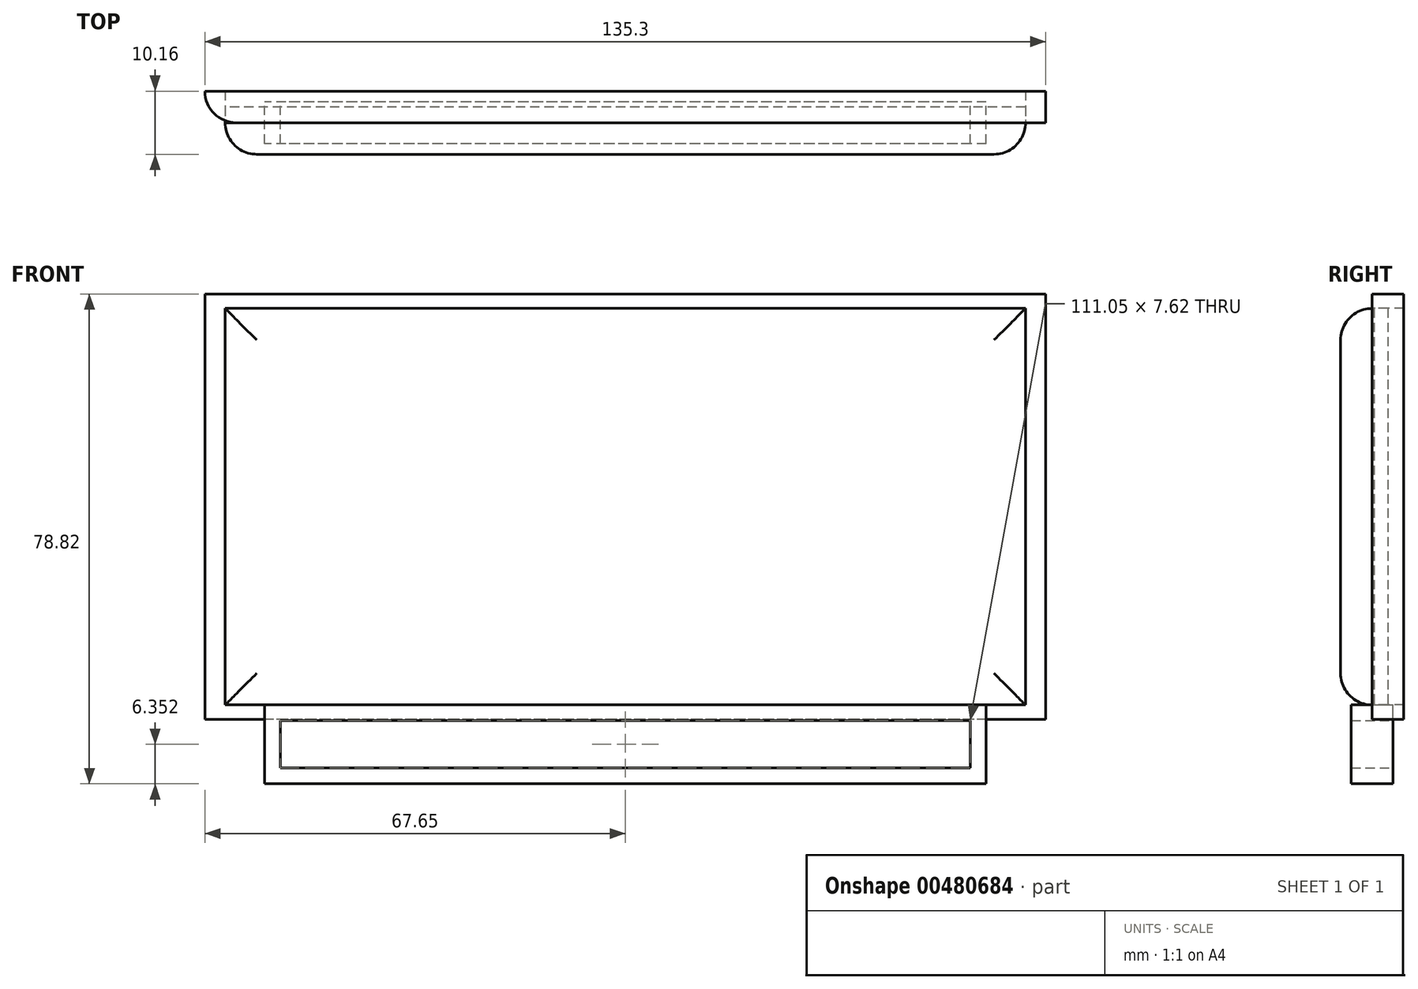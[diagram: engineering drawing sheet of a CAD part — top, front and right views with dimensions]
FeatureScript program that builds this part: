
annotation { "Feature Type Name" : "Feature", "Feature Type Description" : "" }
export const myFeature = defineFeature(function(context is Context, id is Id, definition is map)
    precondition{}
    {
        {
            var Q0;
            Q0=qCreatedBy(makeId("Front.planeOp"),FACE);
            var sketch = newSketch(context, id + "F0", { "sketchPlane" : qUnion([Q0])});
            skLineSegment(sketch, "E0.bottom", {"start": v(67.65, 34.2) * mm, "end": v(-67.65, 34.2) * mm});
            skLineSegment(sketch, "E0.top", {"start": v(67.65, -34.2) * mm, "end": v(-67.65, -34.2) * mm});
            skLineSegment(sketch, "E0.left", {"start": v(67.65, 34.2) * mm, "end": v(67.65, -34.2) * mm});
            skLineSegment(sketch, "E0.right", {"start": v(-67.65, 34.2) * mm, "end": v(-67.65, -34.2) * mm});
            skPoint(sketch, "E0.middle", {"position": v(0, 0) * mm});
            skLineSegment(sketch, "E1.bottom", {"start": v(64.4, 31.9) * mm, "end": v(-64.4, 31.9) * mm});
            skLineSegment(sketch, "E1.top", {"start": v(64.4, -31.9) * mm, "end": v(-64.4, -31.9) * mm});
            skLineSegment(sketch, "E1.left", {"start": v(64.4, 31.9) * mm, "end": v(64.4, -31.9) * mm});
            skLineSegment(sketch, "E1.right", {"start": v(-64.4, 31.9) * mm, "end": v(-64.4, -31.9) * mm});
            skSolve(sketch);
        }
        {
            var Q0;
            Q0=makeQuery(id+"F0.imprint","IMPRINT",FACE,{"disambiguationData":[TD([[makeQuery(id+"F0.imprint","IMPRINT",EDGE,{"derivedFrom":sQuery(id+"F0.wireOp",EDGE,"E1.bottom")}),1.0]])]});
            extrude(context, id + "F1", {"entities" : qUnion([Q0]), "depth" : 5.08 * mm});
        }
        {
            var Q0;
            Q0 = qSketchRegion(id + "F0", true);
            extrude(context, id + "F2", {"entities" : qUnion([Q0]), "oppositeDirection" : true, "depth" : 5.08 * mm});
        }
        {
            var Q0;
            Q0=makeQuery(id+"F1.opExtrude","SWEPT_FACE",FACE,{"disambiguationData":[OSD([sQuery(id+"F0.wireOp",EDGE,"E1.top")])]});
            var sketch = newSketch(context, id + "F3", { "sketchPlane" : qUnion([Q0])});
            skLineSegment(sketch, "E2.bottom", {"start": v(58.07, 3.35) * mm, "end": v(-58.07, 3.35) * mm});
            skLineSegment(sketch, "E2.top", {"start": v(58.07, -3.35) * mm, "end": v(-58.07, -3.35) * mm});
            skLineSegment(sketch, "E2.left", {"start": v(58.07, 3.35) * mm, "end": v(58.07, -3.35) * mm});
            skLineSegment(sketch, "E2.right", {"start": v(-58.07, 3.35) * mm, "end": v(-58.07, -3.35) * mm});
            skPoint(sketch, "E2.middle", {"position": v(0, 0) * mm});
            skSolve(sketch);
        }
        {
            var Q0;
            Q0 = qSketchRegion(id + "F3", true);
            extrude(context, id + "F4", {"entities" : qUnion([Q0]), "depth" : 12.7 * mm});
        }
        {
            var Q0;
            Q0=makeQuery(id+"F4.opExtrude","SWEPT_FACE",FACE,{"disambiguationData":[OSD([sQuery(id+"F3.wireOp",EDGE,"E2.top")])]});
            var Q1;
            Q1=makeQuery(id+"F4.opExtrude","SWEPT_FACE",FACE,{"disambiguationData":[OSD([sQuery(id+"F3.wireOp",EDGE,"E2.bottom")])]});
            shell(context, id + "F5", {"entities" : qUnion([Q0, Q1]), "thickness" : 2.54 * mm});
        }
        {
            var Q0;
            Q0=makeQuery(id+"F1.opExtrude","CAP_FACE",FACE,{"disambiguationData":[OSD([sQuery(id+"F0.wireOp",EDGE,"E1.bottom"),sQuery(id+"F0.wireOp",EDGE,"E1.top"),sQuery(id+"F0.wireOp",EDGE,"E1.left"),sQuery(id+"F0.wireOp",EDGE,"E1.right")])],"isStart":false});
            var Q1;
            Q1=makeQuery(id+"F2.opExtrude","CAP_EDGE",EDGE,{"disambiguationData":[OSD([sQuery(id+"F0.wireOp",EDGE,"E0.right")])],"isStart":true});
            fillet(context, id + "F6", {"entities" : qUnion([Q0, Q1]), "radius" : 5.08 * mm, "tangentPropagation" : true, "allowEdgeOverflow" : false});
        }
        {
            var Q0;
            Q0=makeQuery(id+"F1.opExtrude","CAP_FACE",FACE,{"disambiguationData":[OSD([sQuery(id+"F0.wireOp",EDGE,"E1.bottom"),sQuery(id+"F0.wireOp",EDGE,"E1.top"),sQuery(id+"F0.wireOp",EDGE,"E1.left"),sQuery(id+"F0.wireOp",EDGE,"E1.right")])],"isStart":true});
            extrude(context, id + "F7", {"entities" : qUnion([Q0]), "depth" : 2.54 * mm});
        }
    });
